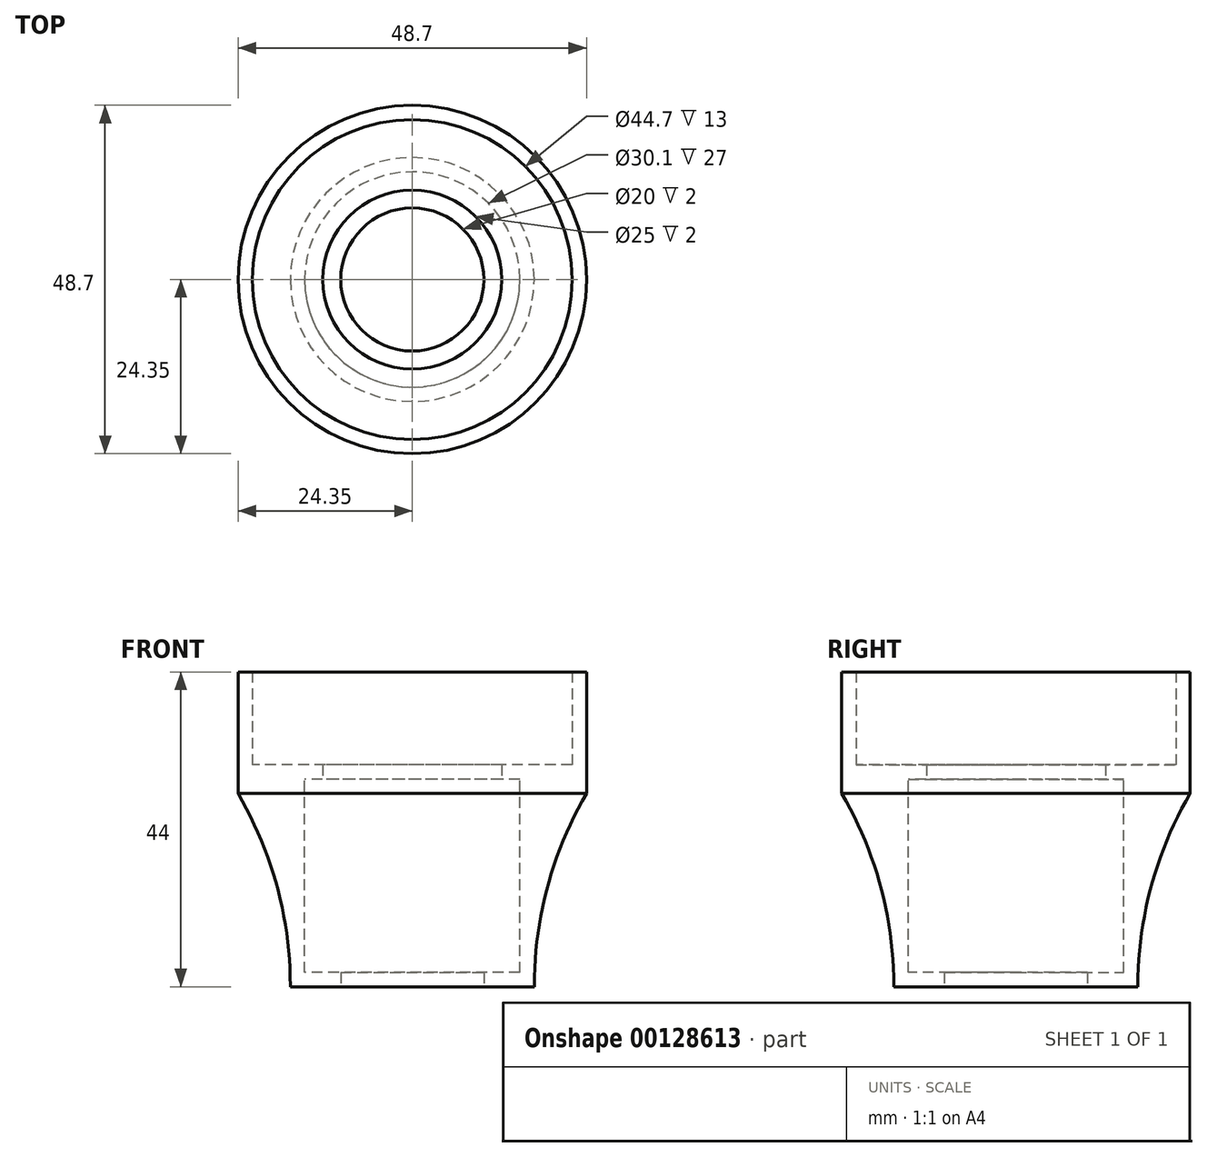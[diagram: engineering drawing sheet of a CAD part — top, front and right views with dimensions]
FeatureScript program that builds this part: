
annotation { "Feature Type Name" : "Feature", "Feature Type Description" : "" }
export const myFeature = defineFeature(function(context is Context, id is Id, definition is map)
    precondition{}
    {
        {
            var Q0;
            Q0=qCreatedBy(makeId("Top.planeOp"),FACE);
            var sketch = newSketch(context, id + "F0", { "sketchPlane" : qUnion([Q0])});
            skCircle(sketch, "E0", {"center": v(0, 0) * mm, "radius": 12.5 * mm});
            skCircle(sketch, "E1", {"center": v(0, 0) * mm, "radius": 24.35 * mm});
            skSolve(sketch);
        }
        {
            var Q0;
            Q0=makeQuery(id+"F0.imprint","IMPRINT",FACE,{"disambiguationData":[TD([[makeQuery(id+"F0.imprint","IMPRINT",EDGE,{"derivedFrom":sQuery(id+"F0.wireOp",EDGE,"E0")}),-1.0]])]});
            var Q1;
            Q1=makeQuery(id+"F0.imprint","IMPRINT",FACE,{"disambiguationData":[TD([[makeQuery(id+"F0.imprint","IMPRINT",EDGE,{"derivedFrom":sQuery(id+"F0.wireOp",EDGE,"E0")}),1.0]])]});
            extrude(context, id + "F1", {"entities" : qUnion([Q0, Q1]), "depth" : 15 * mm, "hasSecondDirection" : true, "secondDirectionOppositeDirection" : true, "secondDirectionDepth" : 2 * mm});
        }
        {
            var Q0;
            Q0=makeQuery(id+"F1.opExtrude","CAP_FACE",FACE,{"disambiguationData":[OSD([sQuery(id+"F0.wireOp",EDGE,"E1")])],"isStart":true});
            var sketch = newSketch(context, id + "F2", { "sketchPlane" : qUnion([Q0])});
            skPoint(sketch, "E2.0", {"position": v(0, 0) * mm});
            skCircle(sketch, "E3", {"center": v(0, 0) * mm, "radius": 17.05 * mm});
            skSolve(sketch);
        }
        {
            var Q0;
            Q0 = qSketchRegion(id + "F2", true);
            extrude(context, id + "F3", {"entities" : qUnion([Q0]), "operationType" : NewBodyOperationType.ADD, "depth" : 27 * mm});
        }
        {
            var Q0;
            Q0=makeQuery(id+"F1.opExtrude","CAP_FACE",FACE,{"disambiguationData":[OSD([sQuery(id+"F0.wireOp",EDGE,"E1")])],"isStart":false});
            shell(context, id + "F4", {"entities" : qUnion([Q0]), "thickness" : 2 * mm});
        }
        {
            var Q0;
            Q0=makeQuery(id+"F3.opExtrude","CAP_FACE",FACE,{"disambiguationData":[OSD([sQuery(id+"F2.wireOp",EDGE,"E3")])],"isStart":false});
            var sketch = newSketch(context, id + "F5", { "sketchPlane" : qUnion([Q0])});
            skPoint(sketch, "E4.0", {"position": v(0, 0) * mm});
            skSolve(sketch);
        }
        {
            var Q0;
            Q0=sQuery(id+"F5.wireOp",VERTEX,"E4.0");
            var Q1;
            Q1=makeQuery(id+"F1.opExtrude","SWEPT_BODY",BODY,{"disambiguationData":[OSD([sQuery(id+"F0.wireOp",EDGE,"E1")])]});
            hole(context, id + "F6", {"style" : HoleStyle.SIMPLE, "endStyle" : HoleEndStyle.THROUGH, "holeDiameter" : 20 * mm, "locations" : qUnion([Q0]), "scope" : qUnion([Q1]), "isTappedThrough" : true});
        }
        {
            var Q0;
            Q0 = qSketchRegion(id + "F0", true);
            extrude(context, id + "F7", {"entities" : qUnion([Q0]), "operationType" : NewBodyOperationType.ADD, "depth" : 2 * mm});
        }
        {
            var Q0;
            Q0=qCreatedBy(makeId("Front.planeOp"),FACE);
            var sketch = newSketch(context, id + "F8", { "sketchPlane" : qUnion([Q0])});
            skArc(sketch, "E5", {"start": v(24.35, -2) * mm, "mid": v(18.9, -15.01) * mm, "end": v(17.05, -29) * mm});
            skPoint(sketch, "E6.0", {"position": v(0, 0) * mm});
            skLineSegment(sketch, "E7", {"start": v(17.05, -2) * mm, "end": v(24.35, -2) * mm});
            skLineSegment(sketch, "E8", {"start": v(17.05, -29) * mm, "end": v(17.05, -2) * mm});
            skLineSegment(sketch, "E9", {"start": v(0, 0) * mm, "end": v(0, -28.74) * mm, "construction": true});
            skSolve(sketch);
        }
        {
            var Q0;
            {var subQ0=sQuery(id+"F8.wireOp",EDGE,"E7");Q0=makeQuery(id+"F8.imprint","IMPRINT",FACE,{"disambiguationData":[TD([[makeQuery(id+"F8.imprint","IMPRINT",EDGE,{"derivedFrom":subQ0}),-1.0]])]});}
            var Q1;
            Q1=sQuery(id+"F8.wireOp",EDGE,"E9");
            revolve(context, id + "F9", {"operationType" : NewBodyOperationType.ADD, "entities" : qUnion([Q0]), "axis" : qUnion([Q1]), "revolveType" : RevolveType.FULL});
        }
    });
